# Revit family: LIRA
name_source: partatom
category: Осветительные приборы
units: mm (PartAtom-declared; Revit-internal decimal feet)

## family parameters
Всегда вертикально = Нет
Источник света = Да
На основе рабочей плоскости = Да
Общий = Нет
При загрузке вырезать с полостями = Нет
Размер круглого соединителя = Использовать диаметр
Тип детали = Нормальный
Точка расчета площади = Да

## types (6) — shared parameters
ADSK_Единица измерения = шт.
ADSK_Завод-изготовитель = ЗАО «Центрстройсвет»
ADSK_Классификация нагрузок = Прочее
ADSK_Количество фаз = 1
ADSK_Количество фаз числовое = 1
ADSK_Коэффициент мощности = 0.92
ADSK_Напряжение = 230 В
ADSK_Ток = 0 А
URL = http://csvt.ru
Видимая форма излучения при визуализации = Нет
Высота = 80 мм
Изготовитель = ЗАО «Центрстройсвет»
Излучение по ширине прямоугольника = 83 мм
Материал коробки = RAL 9006
Материал светильника = RAL 9006
Материал стекла = RAL светящийся
Отметка по умолчанию = 1219 мм
Светофильтр = 16777215
Смещение цветовой температуры при затухании лампы = <Нет>
Угол наклона = 90.00°
Файл фотометрической сетки = LIRA-38_OPAL-1200.ies
Ширина = 87 мм

## per-type parameters (varying)
| type | ADSK_Код изделия | ADSK_Масса | ADSK_Наименование | ADSK_Номинальная мощность | ADSK_Обозначение | ADSK_Полная мощность | Длина | Излучение по длине прямоугольника |
| LIRA-38/OPAL-1200/IP65  (5000К, серый) | ЦБ000009476 | 2.8 | Светодиодный пылевлагозащищенный светильник LIRA-38/OPAL-1200/IP65 (5000К, серый) | 38 Вт | LIRA-38/OPAL-1200/IP65 (5000К, серый) | 41 В·А | 1250 мм | 1230 мм |
| LIRA-38/OPAL-2400/IP65  (5000К, серый) | ЦБ000009477 | 5.5 | Светодиодный пылевлагозащищенный светильник LIRA-38/OPAL-2400/IP65  (5000К, серый) | 38 Вт | LIRA-38/OPAL-2400/IP65  (5000К, серый) | 41 В·А | 2420 мм | 2400 мм |
| LIRA-76/OPAL-2400/IP65  (5000К, серый) | ЦБ000009479 | 5.5 | Светодиодный пылевлагозащищенный светильник LIRA-76/OPAL-2400/IP65  (5000К, серый) | 76 Вт | LIRA-76/OPAL-2400/IP65  (5000К, серый) | 83 В·А | 2420 мм | 2400 мм |
| LIRA-76/OPAL-2400/IP65  (4000К, серый) | ЦБ000009485 | 5.5 | Светодиодный пылевлагозащищенный светильник LIRA-76/OPAL-2400/IP65  (4000К, серый) | 76 Вт | LIRA-76/OPAL-2400/IP65  (4000К, серый) | 83 В·А | 2420 мм | 2400 мм |
| LIRA-38/OPAL-2400/IP65  (4000К, серый) | ЦБ000009484 | 5.5 | Светодиодный пылевлагозащищенный светильник LIRA-38/OPAL-2400/IP65  (4000К, серый) | 38 Вт | LIRA-38/OPAL-2400/IP65  (4000К, серый) | 41 В·А | 2420 мм | 2400 мм |
| LIRA-38/OPAL-1200/IP65  (4000К, серый) | ЦБ000009483 | 2.8 | Светодиодный пылевлагозащищенный светильник LIRA-38/OPAL-1200/IP65  (4000К, серый) | 38 Вт | LIRA-38/OPAL-1200/IP65  (4000К, серый) | 41 В·А | 1250 мм | 1230 мм |
